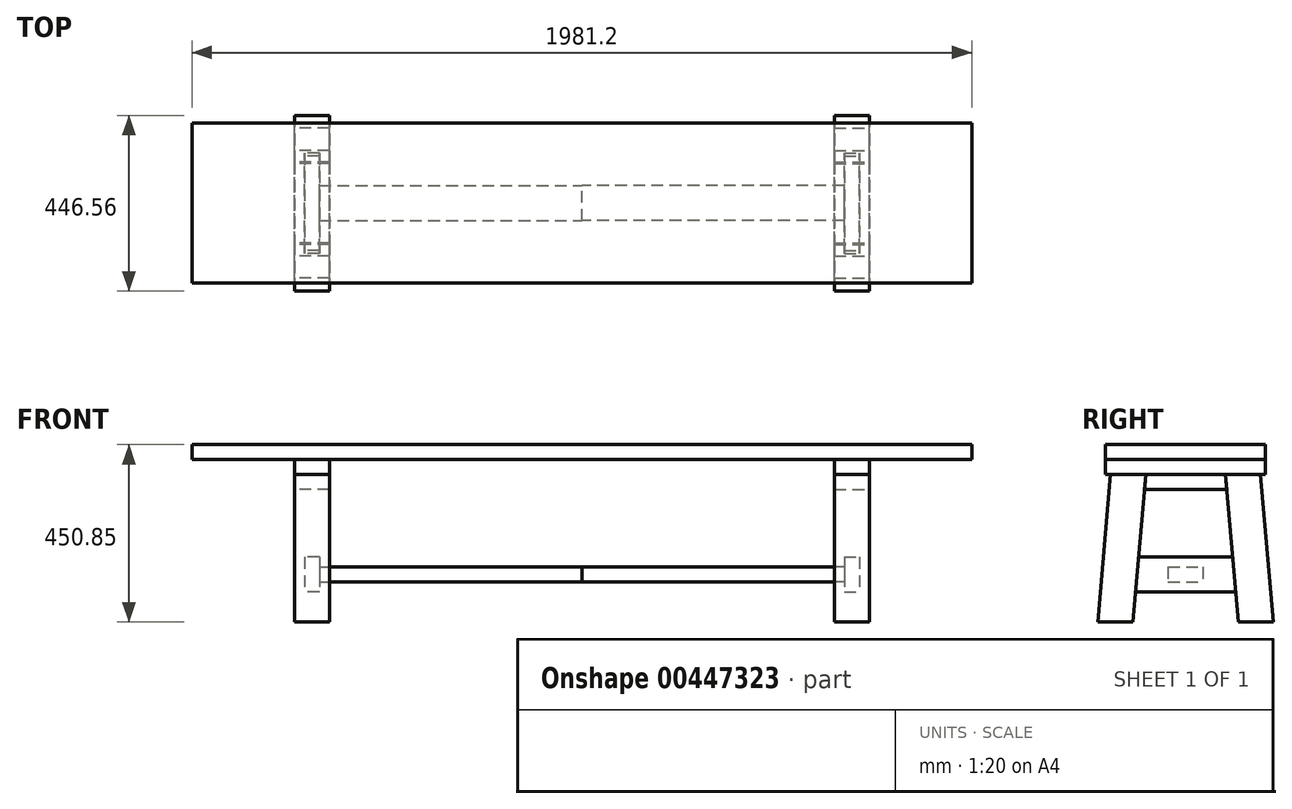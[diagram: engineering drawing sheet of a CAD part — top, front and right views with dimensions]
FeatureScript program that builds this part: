
annotation { "Feature Type Name" : "Feature", "Feature Type Description" : "" }
export const myFeature = defineFeature(function(context is Context, id is Id, definition is map)
    precondition{}
    {
        {
            var Q0;
            Q0=qCreatedBy(makeId("Top.planeOp"),FACE);
            var sketch = newSketch(context, id + "F0", { "sketchPlane" : qUnion([Q0])});
            skLineSegment(sketch, "E0.bottom", {"start": v(990.6, 203.2) * mm, "end": v(-990.6, 203.2) * mm});
            skLineSegment(sketch, "E0.top", {"start": v(990.6, -203.2) * mm, "end": v(-990.6, -203.2) * mm});
            skLineSegment(sketch, "E0.left", {"start": v(990.6, 203.2) * mm, "end": v(990.6, -203.2) * mm});
            skLineSegment(sketch, "E0.right", {"start": v(-990.6, 203.2) * mm, "end": v(-990.6, -203.2) * mm});
            skPoint(sketch, "E0.middle", {"position": v(0, 0) * mm});
            skSolve(sketch);
        }
        {
            var Q0;
            Q0 = qSketchRegion(id + "F0", true);
            extrude(context, id + "F1", {"entities" : qUnion([Q0]), "depth" : 38.1 * mm});
        }
        {
            var Q0;
            Q0=qCreatedBy(makeId("Right.planeOp"),FACE);
            cPlane(context, id + "F2", {"entities" : qUnion([Q0]), "cplaneType" : CPlaneType.OFFSET, "offset" : 685.8 * mm, "oppositeDirection" : true, "width" : 152.4 * mm, "height" : 152.4 * mm});
        }
        {
            var Q0;
            Q0=makeQuery(id+"F1.opExtrude","CAP_FACE",FACE,{"disambiguationData":[OSD([sQuery(id+"F0.wireOp",EDGE,"E0.bottom"),sQuery(id+"F0.wireOp",EDGE,"E0.top"),sQuery(id+"F0.wireOp",EDGE,"E0.left"),sQuery(id+"F0.wireOp",EDGE,"E0.right")])],"isStart":true});
            var sketch = newSketch(context, id + "F3", { "sketchPlane" : qUnion([Q0])});
            skLineSegment(sketch, "E1", {"start": v(0, 0) * mm, "end": v(0, -125.79) * mm, "construction": true});
            skLineSegment(sketch, "E2", {"start": v(0, 0) * mm, "end": v(-157.82, 0) * mm, "construction": true});
            skLineSegment(sketch, "E3.bottom", {"start": v(-730.25, 203.2) * mm, "end": v(-641.35, 203.2) * mm});
            skLineSegment(sketch, "E3.top", {"start": v(-730.25, -203.2) * mm, "end": v(-641.35, -203.2) * mm});
            skLineSegment(sketch, "E3.left", {"start": v(-730.25, 203.2) * mm, "end": v(-730.25, -203.2) * mm});
            skLineSegment(sketch, "E3.right", {"start": v(-641.35, 203.2) * mm, "end": v(-641.35, -203.2) * mm});
            skLineSegment(sketch, "E4", {"start": v(-685.8, 105.66) * mm, "end": v(-685.8, -124.13) * mm, "construction": true});
            skSolve(sketch);
        }
        {
            var Q0;
            Q0 = qSketchRegion(id + "F3", true);
            extrude(context, id + "F4", {"entities" : qUnion([Q0]), "depth" : 38.1 * mm});
        }
        {
            var Q0;
            Q0=qCreatedBy(id+"F2.planeOp",FACE);
            var sketch = newSketch(context, id + "F5", { "sketchPlane" : qUnion([Q0])});
            skLineSegment(sketch, "E5", {"start": v(190.5, -38.1) * mm, "end": v(223.28, -412.75) * mm});
            skLineSegment(sketch, "E6", {"start": v(223.28, -412.75) * mm, "end": v(134.04, -412.75) * mm});
            skLineSegment(sketch, "E7", {"start": v(134.04, -412.75) * mm, "end": v(101.26, -38.1) * mm});
            skLineSegment(sketch, "E8", {"start": v(101.26, -38.1) * mm, "end": v(190.5, -38.1) * mm});
            skLineSegment(sketch, "E9", {"start": v(0, 0) * mm, "end": v(0, 61.26) * mm, "construction": true});
            skLineSegment(sketch, "E10.MirrorCS", {"start": v(-190.5, -38.1) * mm, "end": v(-223.28, -412.75) * mm});
            skLineSegment(sketch, "E11.MirrorCS", {"start": v(-223.28, -412.75) * mm, "end": v(-134.04, -412.75) * mm});
            skLineSegment(sketch, "E12.MirrorCS", {"start": v(-134.04, -412.75) * mm, "end": v(-101.26, -38.1) * mm});
            skLineSegment(sketch, "E13.MirrorCS", {"start": v(-101.26, -38.1) * mm, "end": v(-190.5, -38.1) * mm});
            skSolve(sketch);
        }
        {
            var Q0;
            Q0 = qSketchRegion(id + "F5", true);
            extrude(context, id + "F6", {"entities" : qUnion([Q0]), "endBound" : BoundingType.SYMMETRIC, "depth" : 88.9 * mm});
        }
        {
            var Q0;
            Q0=qCreatedBy(id+"F2.planeOp",FACE);
            var sketch = newSketch(context, id + "F7", { "sketchPlane" : qUnion([Q0])});
            skLineSegment(sketch, "E14", {"start": v(101.26, -38.1) * mm, "end": v(104.6, -76.2) * mm});
            skLineSegment(sketch, "E15", {"start": v(104.6, -76.2) * mm, "end": v(-104.6, -76.2) * mm});
            skLineSegment(sketch, "E16", {"start": v(-104.6, -76.2) * mm, "end": v(-101.26, -38.1) * mm});
            skLineSegment(sketch, "E17", {"start": v(-101.26, -38.1) * mm, "end": v(101.26, -38.1) * mm});
            skSolve(sketch);
        }
        {
            var Q0;
            Q0 = qSketchRegion(id + "F7", true);
            extrude(context, id + "F8", {"entities" : qUnion([Q0]), "endBound" : BoundingType.SYMMETRIC, "depth" : 88.9 * mm});
        }
        {
            var Q0;
            Q0=qCreatedBy(id+"F2.planeOp",FACE);
            var sketch = newSketch(context, id + "F9", { "sketchPlane" : qUnion([Q0])});
            skLineSegment(sketch, "E18", {"start": v(119.6, -247.65) * mm, "end": v(127.37, -336.55) * mm});
            skLineSegment(sketch, "E19", {"start": v(127.37, -336.55) * mm, "end": v(-127.37, -336.55) * mm});
            skLineSegment(sketch, "E20", {"start": v(-127.37, -336.55) * mm, "end": v(-119.6, -247.65) * mm});
            skLineSegment(sketch, "E21", {"start": v(-119.6, -247.65) * mm, "end": v(119.6, -247.65) * mm});
            skSolve(sketch);
        }
        {
            var Q0;
            Q0 = qSketchRegion(id + "F9", true);
            extrude(context, id + "F10", {"entities" : qUnion([Q0]), "endBound" : BoundingType.SYMMETRIC, "depth" : 38.1 * mm});
        }
        {
            var Q0;
            Q0=qCreatedBy(makeId("Front.planeOp"),FACE);
            var sketch = newSketch(context, id + "F11", { "sketchPlane" : qUnion([Q0])});
            skLineSegment(sketch, "E22.bottom", {"start": v(-666.75, -273.05) * mm, "end": v(0, -273.05) * mm});
            skLineSegment(sketch, "E22.top", {"start": v(-666.75, -311.15) * mm, "end": v(0, -311.15) * mm});
            skLineSegment(sketch, "E22.left", {"start": v(-666.75, -273.05) * mm, "end": v(-666.75, -311.15) * mm});
            skLineSegment(sketch, "E22.right", {"start": v(0, -273.05) * mm, "end": v(0, -311.15) * mm});
            skLineSegment(sketch, "E23", {"start": v(-666.75, -292.1) * mm, "end": v(-704.85, -292.1) * mm, "construction": true});
            skSolve(sketch);
        }
        {
            var Q0;
            Q0 = qSketchRegion(id + "F11", true);
            extrude(context, id + "F12", {"entities" : qUnion([Q0]), "endBound" : BoundingType.SYMMETRIC, "depth" : 88.9 * mm});
        }
        {
            var Q0;
            Q0=makeQuery(id+"F6.opExtrude","SWEPT_BODY",BODY,{"disambiguationData":[OSD([sQuery(id+"F5.wireOp",EDGE,"E5"),sQuery(id+"F5.wireOp",EDGE,"E6"),sQuery(id+"F5.wireOp",EDGE,"E7"),sQuery(id+"F5.wireOp",EDGE,"E8")])]});
            var Q1;
            Q1=makeQuery(id+"F6.opExtrude","SWEPT_BODY",BODY,{"disambiguationData":[OSD([sQuery(id+"F5.wireOp",EDGE,"E10.MirrorCS"),sQuery(id+"F5.wireOp",EDGE,"E11.MirrorCS"),sQuery(id+"F5.wireOp",EDGE,"E12.MirrorCS"),sQuery(id+"F5.wireOp",EDGE,"E13.MirrorCS")])]});
            var Q2;
            Q2=makeQuery(id+"F8.opExtrude","SWEPT_BODY",BODY,{"disambiguationData":[OSD([sQuery(id+"F7.wireOp",EDGE,"E14"),sQuery(id+"F7.wireOp",EDGE,"E15"),sQuery(id+"F7.wireOp",EDGE,"E16"),sQuery(id+"F7.wireOp",EDGE,"E17")])]});
            var Q3;
            Q3=makeQuery(id+"F10.opExtrude","SWEPT_BODY",BODY,{"disambiguationData":[OSD([sQuery(id+"F9.wireOp",EDGE,"E18"),sQuery(id+"F9.wireOp",EDGE,"E19"),sQuery(id+"F9.wireOp",EDGE,"E20"),sQuery(id+"F9.wireOp",EDGE,"E21")])]});
            var Q4;
            Q4=makeQuery(id+"F12.opExtrude","SWEPT_BODY",BODY,{"disambiguationData":[OSD([sQuery(id+"F11.wireOp",EDGE,"gA5lbltU-snL0-JIuX-GtOt-TWmjrxMTRiP5"),sQuery(id+"F11.wireOp",EDGE,"qAJlOmav-kImi-jJFV-oGYb-r5wZl8YZniuD"),sQuery(id+"F11.wireOp",EDGE,"DoZrSelB-DMcr-G7h3-ZlVq-dsrTDpjcbj6s"),sQuery(id+"F11.wireOp",EDGE,"D3dEJJVD-ggTt-ViF7-emZf-wlJigWkUbVqv")])]});
            var Q5;
            Q5=makeQuery(id+"F12.opExtrude","SWEPT_BODY",BODY,{"disambiguationData":[OSD([sQuery(id+"F11.wireOp",EDGE,"E22.bottom"),sQuery(id+"F11.wireOp",EDGE,"E22.top"),sQuery(id+"F11.wireOp",EDGE,"E22.left"),sQuery(id+"F11.wireOp",EDGE,"E22.right")])]});
            var Q6;
            Q6=makeQuery(id+"F4.opExtrude","SWEPT_BODY",BODY,{"disambiguationData":[OSD([sQuery(id+"F3.wireOp",EDGE,"E3.bottom"),sQuery(id+"F3.wireOp",EDGE,"E3.top"),sQuery(id+"F3.wireOp",EDGE,"E3.left"),sQuery(id+"F3.wireOp",EDGE,"E3.right")])]});
            var Q7;
            Q7=qCreatedBy(makeId("Right.planeOp"),FACE);
            mirror(context, id + "F13", {"entities" : qUnion([Q0, Q1, Q2, Q3, Q4, Q5, Q6]), "mirrorPlane" : qUnion([Q7])});
        }
    });
